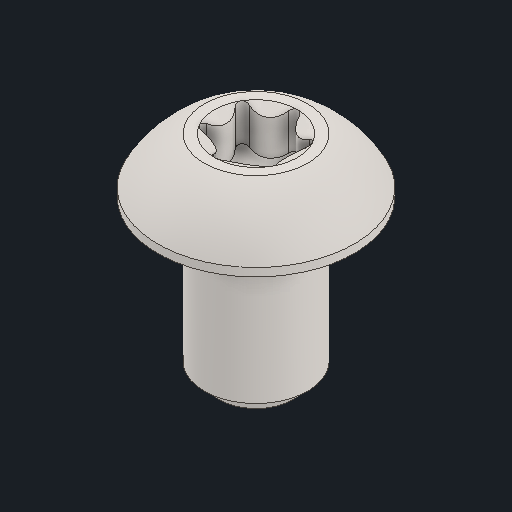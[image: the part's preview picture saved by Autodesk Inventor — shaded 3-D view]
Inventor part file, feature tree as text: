
AUTODESK INVENTOR PART (.ipt)
format: ipt  version: 2024 (Build 280153000, 153)  size: 189,952 bytes
history: native  units: in
note: dims shown in document units (in); Inventor stores cm internally (conversion verified against a paired STEP export)
features: chamfer x1
ambient origin geometry x8: Origin, YZ Plane, XZ Plane, XY Plane, X Axis, Y Axis, Z Axis, Center Point
bodies: Solid1 (feature_tree)
feature tree (1):
  chamfer  "Chamfer2"  [1 undecoded]
note: 1 required parameter value undecoded (feature->parameter linkage not recoverable at this tier; creation-order binding heuristic only, values carry confidence <= 0.55)
